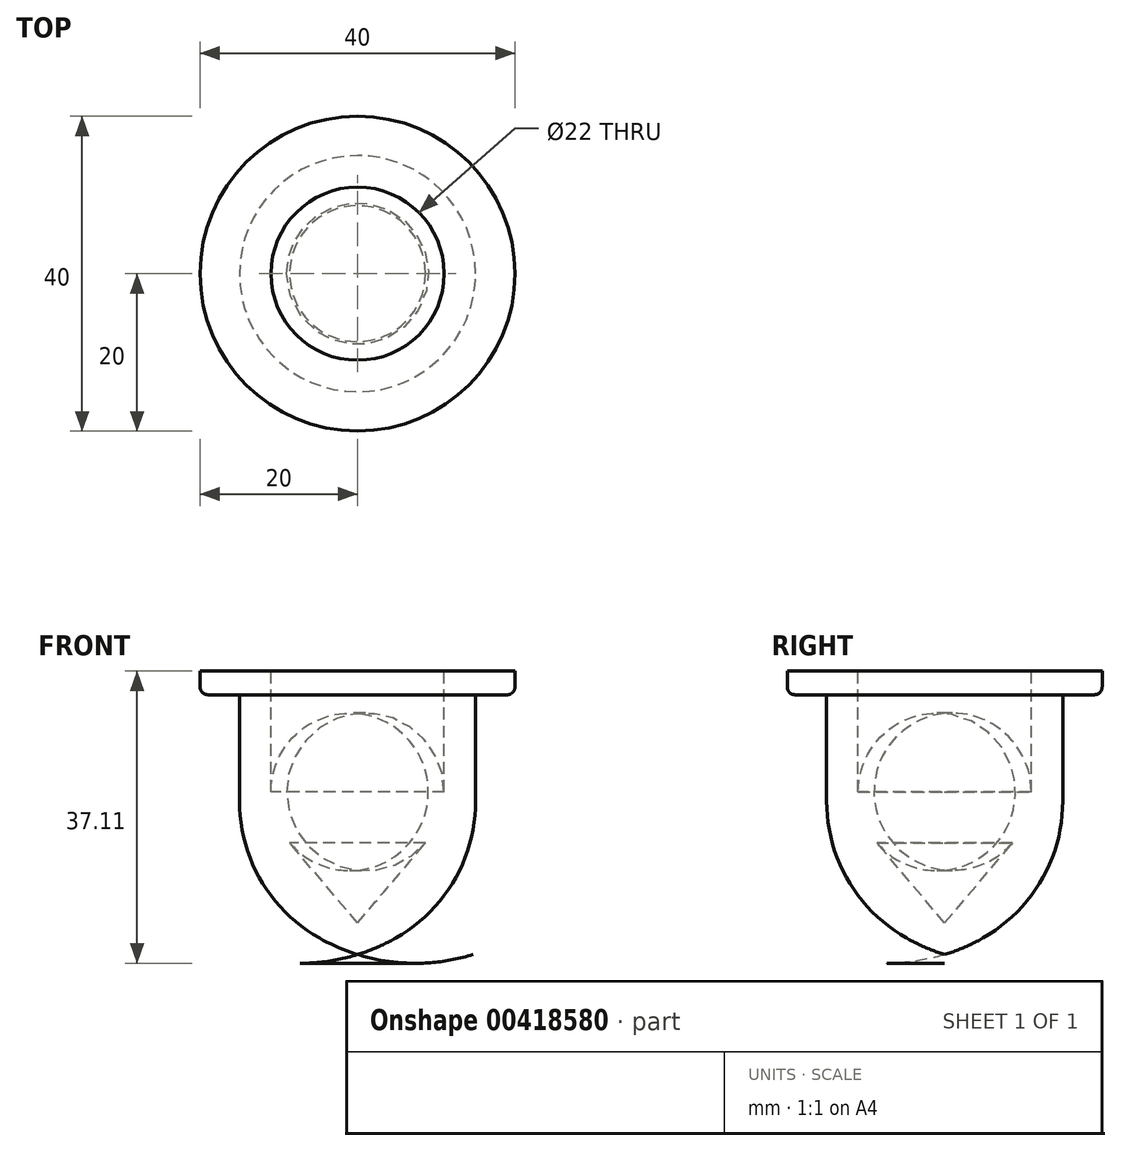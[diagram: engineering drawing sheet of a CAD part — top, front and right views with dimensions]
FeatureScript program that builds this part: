
annotation { "Feature Type Name" : "Feature", "Feature Type Description" : "" }
export const myFeature = defineFeature(function(context is Context, id is Id, definition is map)
    precondition{}
    {
        {
            var Q0;
            Q0=qCreatedBy(makeId("Front.planeOp"),FACE);
            var sketch = newSketch(context, id + "F0", { "sketchPlane" : qUnion([Q0])});
            skLineSegment(sketch, "E0", {"start": v(0, 0) * mm, "end": v(15, 0) * mm, "construction": true});
            skLineSegment(sketch, "E1", {"start": v(0, 0) * mm, "end": v(0, -20) * mm, "construction": true});
            skLineSegment(sketch, "E2", {"start": v(15, 0) * mm, "end": v(19, 0) * mm});
            skLineSegment(sketch, "E3", {"start": v(20, 1) * mm, "end": v(20, 3) * mm});
            skLineSegment(sketch, "E4", {"start": v(11, 3) * mm, "end": v(11, -12.34) * mm});
            skLineSegment(sketch, "E5", {"start": v(15, -13.5) * mm, "end": v(15, 0) * mm});
            skPoint(sketch, "E6.visualSharp", {"position": v(20, 0) * mm});
            skArc(sketch, "E6.filletArc", {"start": v(19, 0) * mm, "mid": v(19.7, 0.3) * mm, "end": v(20, 1) * mm});
            skArc(sketch, "E7", {"start": v(0, -33) * mm, "mid": v(2.49, -32.08) * mm, "end": v(4.86, -30.9) * mm});
            skPoint(sketch, "E8.visualSharp", {"position": v(11, -16) * mm});
            skPoint(sketch, "E9.visualSharp", {"position": v(15, -20) * mm});
            skArc(sketch, "E9.filletArc", {"start": v(4.86, -30.9) * mm, "mid": v(12.28, -23.57) * mm, "end": v(15, -13.5) * mm});
            skLineSegment(sketch, "E10", {"start": v(0, -29) * mm, "end": v(0, -33) * mm});
            skLineSegment(sketch, "E11", {"start": v(8.63, -18.8) * mm, "end": v(0, -29) * mm});
            skArc(sketch, "E12.filletArc", {"start": v(8.63, -18.8) * mm, "mid": v(10.39, -15.78) * mm, "end": v(11, -12.34) * mm});
            skLineSegment(sketch, "E13", {"start": v(11, 3) * mm, "end": v(20, 3) * mm});
            skSolve(sketch);
        }
        {
            var Q0;
            Q0=makeQuery(id+"F0.imprint","IMPRINT",FACE,{"disambiguationData":[TD([[makeQuery(id+"F0.imprint","IMPRINT",EDGE,{"derivedFrom":sQuery(id+"F0.wireOp",EDGE,"E2")}),1.0]])]});
            var Q1;
            Q1=sQuery(id+"F0.wireOp",EDGE,"E1");
            revolve(context, id + "F1", {"entities" : qUnion([Q0]), "axis" : qUnion([Q1]), "revolveType" : RevolveType.FULL});
        }
    });
